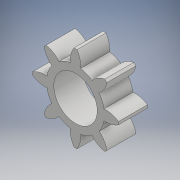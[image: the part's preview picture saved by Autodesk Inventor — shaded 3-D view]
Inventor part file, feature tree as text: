
AUTODESK INVENTOR PART (.ipt)
format: ipt  version: 2018 (Build 220112000, 112)  size: 330,752 bytes
history: native  units: mm
features: extrude x2, sketch x2, pattern_circular x1
ambient origin geometry x8: Origin, YZ Plane, XZ Plane, XY Plane, X Axis, Y Axis, Z Axis, Center Point
bodies: Solid1 (feature_tree)
feature tree (5):
  extrude  "Extrusion1"  Depth=4.0mm
  extrude  "Extrusion2"  Depth=2.0mm
  pattern_circular  "Circular Pattern1"  [2 undecoded]
  sketch  "Sketch1"  dims[d0=3.0mm d1=4.0mm]
  sketch  "Sketch2"  dims[d2=2.0mm d3=0.0mm d4=0.2mm d5=0.35mm d6=90.0deg d7=0.7mm d8=1.541mm d9=2.0mm d10=0.0mm d11=80.0mm d12=360.0deg]
note: 2 required parameter values undecoded (feature->parameter linkage not recoverable at this tier; creation-order binding heuristic only, values carry confidence <= 0.55)
